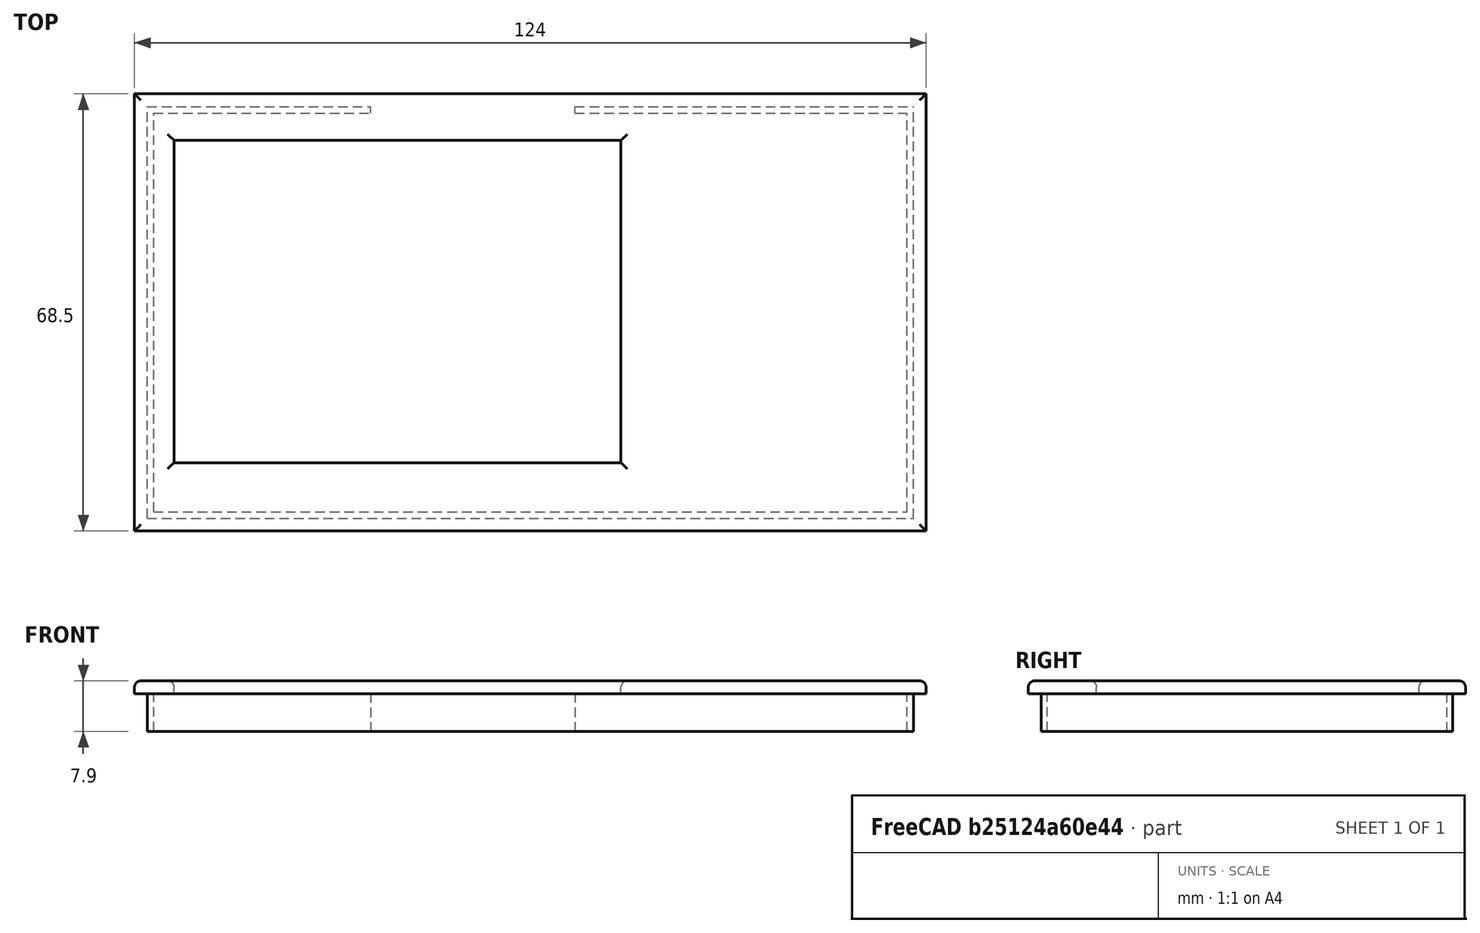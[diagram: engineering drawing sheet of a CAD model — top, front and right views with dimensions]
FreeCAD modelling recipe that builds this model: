
FCSTD DOCUMENT  (FreeCAD 0.17R13541 (Git))
Label: IR top cover
License: All rights reserved
LicenseURL: http://en.wikipedia.org/wiki/All_rights_reserved
objects: Part::Box×5, Part::Cut×3, Part::Fillet×2
note: 10 computed .brp shape members not serialized (recipe doc carries the construction recipe); baked Part::Feature solids carry a one-line shape summary decoded from their .brp

FEATURE [Part::Box] Box  label="Cube"
  AttacherType = Attacher::AttachEngine3D
  Height = 6
  Length = 120
  Width = 64.5
FEATURE [Part::Box] Box001  label="Cube001"
  AttacherType = Attacher::AttachEngine3D
  Height = 2
  Length = 124
  Placement = pos=(-2,-2,6) rot=(0,0,1;0rad)
  Width = 68.5
FEATURE [Part::Box] Box002  label="Cube002"
  AttacherType = Attacher::AttachEngine3D
  Height = 6
  Length = 118
  Placement = pos=(1,1,0) rot=(0,0,1;0rad)
  Width = 62.5
FEATURE [Part::Cut] Cut
  Base = -> Box
  Tool = -> Box002
FEATURE [Part::Box] Box003  label="Cube003"
  AttacherType = Attacher::AttachEngine3D
  Height = 10
  Length = 32
  Placement = pos=(35,58,-1) rot=(0,0,1;0rad)
  Width = 10
FEATURE [Part::Cut] Cut001
  Base = -> Cut
  Placement = pos=(0,0,0.1) rot=(0,0,1;0rad)
  Tool = -> Box003
FEATURE [Part::Box] Box004  label="Cube004"
  AttacherType = Attacher::AttachEngine3D
  Height = 10
  Length = 70
  Placement = pos=(4.2,8.7,0) rot=(0,0,1;0rad)
  Width = 50.5
FEATURE [Part::Cut] Cut002
  Base = -> Box001
  Tool = -> Box004
FEATURE [Part::Fillet] Fillet
  Base = -> Cut002
  Edges = 4 edges r=1: [Edge10,Edge11,Edge12,Edge13]
FEATURE [Part::Fillet] Fillet001
  Base = -> Fillet
  Edges = 4 edges r=1: [Edge5,Edge6,Edge7,Edge8]
